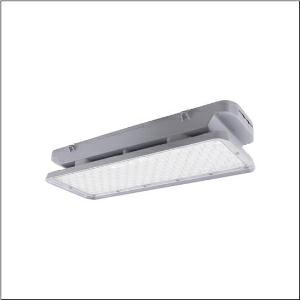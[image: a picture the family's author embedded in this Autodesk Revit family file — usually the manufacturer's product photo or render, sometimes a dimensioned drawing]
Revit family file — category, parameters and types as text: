
# Revit family: highbay_21-s_51hk41da4jca
name_source: partatom
category: Lighting Fixtures
units: mm (PartAtom-declared; Revit-internal decimal feet)

## family parameters
Cut with Voids When Loaded = No
Host = Face
Light Source = No
Part Type = Normal
Room Calculation Point = No
Round Connector Dimension = Use Diameter
Shared = No

## types (1)
- Highbay 21-S (1 x LED, 19100 lm, 107 W, 4000K)
    Apparent Load = 107 VA
    CIE Flux Codes = 87 97 99 100 100
    Color Rendering = 80
    Color Temperature = 4000K
    Default Elevation = 1800 mm
    Description = Highbay 21-S, LED high bay luminaire, primary light control with lens, of PC, primary optical cover: cover panel, light emission: direct distribution, primary light characteristic: symmetric, installation type: suspended mounting, surface-mounted, LED, rated luminous flux: 19.100lm, luminous efficacy: 159lm/W, light colour: 840, colour temperature: 4000K, control gear: ECG DALI, with terminal, 5-pole, max. 2.5mm², mains connection: 220..240V, AC, 50Hz, rated input power: 120W, housing, of diecast aluminium, coated, grey, length: 471mm, width: 172mm, height: 87mm, protection rating (complete): IP66, insulation class (complete): insulation class I (protective earthing), certification: CE, ENEC, UKCA, protection symbol: D, impact resistance: IK08, permissible operating ambient temperature: -30..+55°C, corresponds to IFS (International Featured Standards) requirements for safety and quality in the food industry, LABS conformity tested according to VDMA 24364:2018-05, packaging unit: 1 piece
    Height = 89 mm
    Lamp = 1 x LED
    Lamp Light Flux = 19100 lm
    Lamp Power = 107 W
    Lamp count = 1
    Length = 471 mm
    Luminous efficacy = 179 lm/W
    Manufacturer = Siteco
    ModVariant = No
    Model = 51HK41DA4JCA
    Mounting Place = Ceiling
    Mounting Type = Pendant
    Number of Poles = 1
    OnlyDefault = Yes
    Power Factor = 1
    Product Name = Highbay 21-S
    Product group = LED high bay luminaire
    ProductGroupID = 903
    Protection Class = Protection class I
    Protection Degree = IP 66
    RLX_Detail_Level = 1
    RLX_Emergency_Light_Flux = 0 lm
    RLX_Emergency_Type = 0
    RLX_Emergency_Type_DB = No
    RlxData = <blob elided: 21537 chars, md5=ddf6fe07>
    Socket = socket
    Standby Power = 0 W
    System Light Flux = 19100 lm
    System Power = 107 W
    Type Comments = Product without accessories
    Type Image = l_1276526.jpg
    URL = http://relux.com
    VarID = ---
    Voltage = 0 V
    Weight = 0.00 kg
    Width = 172 mm

## geometry (parser evidence)
native form markers: Blend x4, Sweep x11
no freeform markers — native parametric forms only
